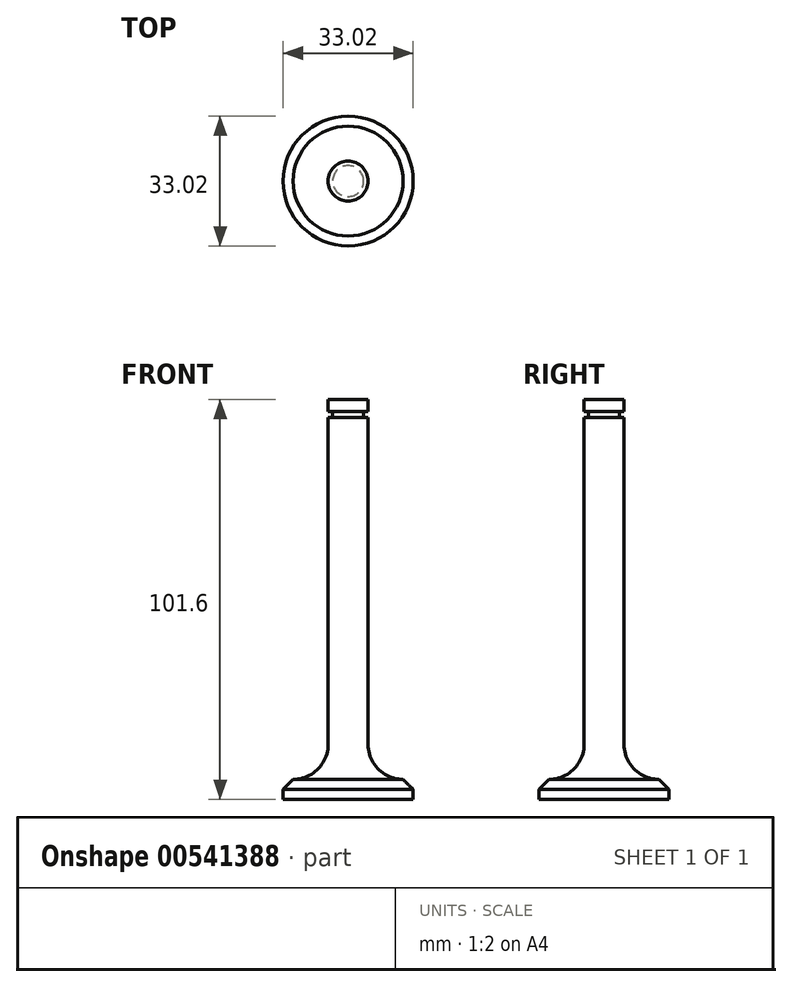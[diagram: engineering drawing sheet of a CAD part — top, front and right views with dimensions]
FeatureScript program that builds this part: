
annotation { "Feature Type Name" : "Feature", "Feature Type Description" : "" }
export const myFeature = defineFeature(function(context is Context, id is Id, definition is map)
    precondition{}
    {
        {
            var Q0;
            Q0=qCreatedBy(makeId("Front.planeOp"),FACE);
            var sketch = newSketch(context, id + "F0", { "sketchPlane" : qUnion([Q0])});
            skLineSegment(sketch, "E0", {"start": v(-16.51, -6.1) * mm, "end": v(-16.51, -3.55) * mm});
            skLineSegment(sketch, "E1", {"start": v(-16.51, -6.1) * mm, "end": v(0, -6.1) * mm});
            skLineSegment(sketch, "E2", {"start": v(-16.51, -3.55) * mm, "end": v(-13.97, -1.01) * mm});
            skLineSegment(sketch, "E3", {"start": v(-13.97, -1.01) * mm, "end": v(-13.97, -1.01) * mm});
            skLineSegment(sketch, "E4", {"start": v(-5.08, 7.88) * mm, "end": v(-5.08, 90.91) * mm});
            skLineSegment(sketch, "E5", {"start": v(-5.08, 90.91) * mm, "end": v(-3.94, 90.91) * mm});
            skLineSegment(sketch, "E6", {"start": v(-3.94, 90.91) * mm, "end": v(-3.94, 92.46) * mm});
            skLineSegment(sketch, "E7", {"start": v(-3.94, 92.46) * mm, "end": v(-5.08, 92.46) * mm});
            skLineSegment(sketch, "E8", {"start": v(-5.08, 92.46) * mm, "end": v(-5.08, 95.5) * mm});
            skLineSegment(sketch, "E9", {"start": v(-5.08, 95.5) * mm, "end": v(0, 95.5) * mm});
            skPoint(sketch, "E10.visualSharp", {"position": v(-5.08, -1.01) * mm});
            skArc(sketch, "E10.filletArc", {"start": v(-13.97, -1.01) * mm, "mid": v(-7.68, 1.6) * mm, "end": v(-5.08, 7.88) * mm});
            skLineSegment(sketch, "E11", {"start": v(0, 95.5) * mm, "end": v(0, -6.1) * mm});
            skSolve(sketch);
        }
        {
            var Q0;
            Q0=makeQuery(id+"F0.imprint","IMPRINT",FACE,{"disambiguationData":[TD([[makeQuery(id+"F0.imprint","IMPRINT",EDGE,{"derivedFrom":sQuery(id+"F0.wireOp",EDGE,"E0")}),-1.0]])]});
            var Q1;
            Q1=sQuery(id+"F0.wireOp",EDGE,"E11");
            revolve(context, id + "F1", {"entities" : qUnion([Q0]), "axis" : qUnion([Q1]), "revolveType" : RevolveType.FULL});
        }
    });
